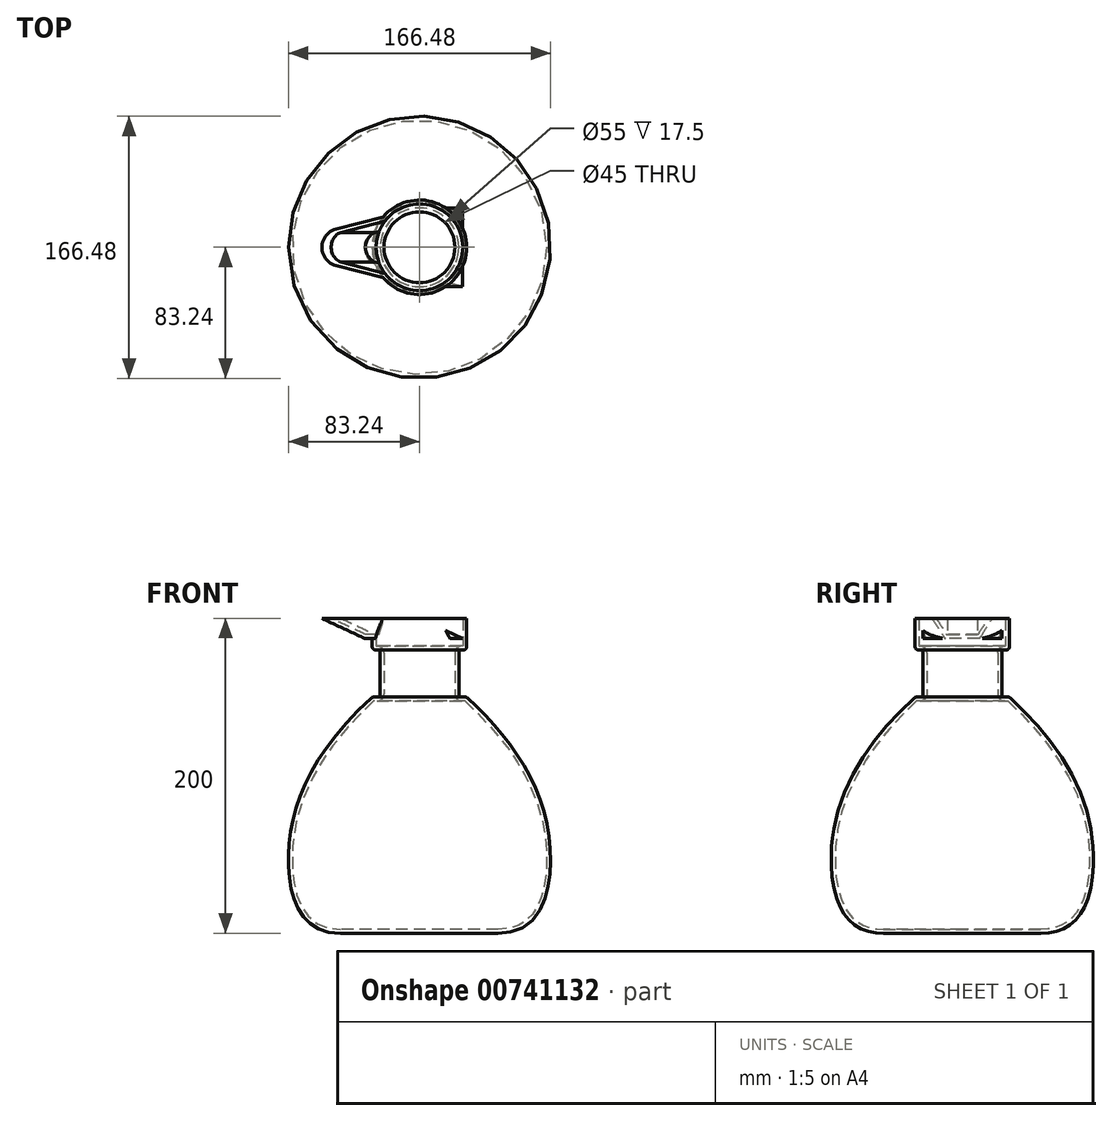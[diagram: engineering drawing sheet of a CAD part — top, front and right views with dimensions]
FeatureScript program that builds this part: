
annotation { "Feature Type Name" : "Feature", "Feature Type Description" : "" }
export const myFeature = defineFeature(function(context is Context, id is Id, definition is map)
    precondition{}
    {
        {
            var Q0;
            Q0=qCreatedBy(makeId("Front.planeOp"),FACE);
            var sketch = newSketch(context, id + "F0", { "sketchPlane" : qUnion([Q0])});
            skLineSegment(sketch, "E0", {"start": v(50, 0) * mm, "end": v(0, 0) * mm});
            skLineSegment(sketch, "E1", {"start": v(0, 0) * mm, "end": v(0, 200) * mm});
            skLineSegment(sketch, "E2", {"start": v(0, 200) * mm, "end": v(30, 200) * mm});
            skLineSegment(sketch, "E3", {"start": v(30, 200) * mm, "end": v(30, 180) * mm});
            skLineSegment(sketch, "E4", {"start": v(30, 180) * mm, "end": v(25, 180) * mm});
            skLineSegment(sketch, "E5", {"start": v(25, 180) * mm, "end": v(25, 150) * mm});
            skLineSegment(sketch, "E6", {"start": v(25, 150) * mm, "end": v(30, 150) * mm});
            skFitSpline(sketch, "E7", {"points": [v(30, 150) * mm, v(83.24, 45.92) * mm, v(50, 0) * mm], "startDerivative": vector(202.96, -186.52) * mm, "endDerivative": vector(-190.27, 0) * mm});
            skSolve(sketch);
        }
        {
            var Q0;
            Q0 = qSketchRegion(id + "F0", true);
            var Q1;
            Q1=sQuery(id+"F0.wireOp",EDGE,"E1");
            revolve(context, id + "F1", {"surfaceOperationType" : NewSurfaceOperationType.NEW, "entities" : qUnion([Q0]), "axis" : qUnion([Q1]), "revolveType" : RevolveType.FULL});
        }
        {
            var Q0;
            Q0=makeQuery(id+"F1.opRevolve","SWEPT_EDGE",EDGE,{"disambiguationData":[OSD([sQuery(id+"F0.wireOp",EDGE,"E3"),sQuery(id+"F0.wireOp",EDGE,"E4")])]});
            var Q1;
            Q1=makeQuery(id+"F1.opRevolve","SWEPT_EDGE",EDGE,{"disambiguationData":[OSD([sQuery(id+"F0.wireOp",EDGE,"E4"),sQuery(id+"F0.wireOp",EDGE,"E5")])]});
            var Q2;
            Q2=makeQuery(id+"F1.opRevolve","SWEPT_EDGE",EDGE,{"disambiguationData":[OSD([sQuery(id+"F0.wireOp",EDGE,"E6"),sQuery(id+"F0.wireOp",EDGE,"E7")])]});
            var Q3;
            Q3=makeQuery(id+"F1.opRevolve","SWEPT_EDGE",EDGE,{"disambiguationData":[OSD([sQuery(id+"F0.wireOp",EDGE,"E5"),sQuery(id+"F0.wireOp",EDGE,"E6")])]});
            fillet(context, id + "F2", {"entities" : qUnion([Q0, Q1, Q2, Q3]), "radius" : 2 * mm, "tangentPropagation" : true, "allowEdgeOverflow" : false});
        }
        {
            var Q0;
            Q0=makeQuery(id+"F1.opRevolve","SWEPT_FACE",FACE,{"disambiguationData":[OSD([sQuery(id+"F0.wireOp",EDGE,"E2")])]});
            var sketch = newSketch(context, id + "F3", { "sketchPlane" : qUnion([Q0])});
            skArc(sketch, "E8", {"start": v(-62, 0) * mm, "mid": v(-59.47, -7.37) * mm, "end": v(-52.94, -11.63) * mm});
            skLineSegment(sketch, "E9", {"start": v(0, 0) * mm, "end": v(0, -25) * mm});
            skLineSegment(sketch, "E10", {"start": v(0, -25) * mm, "end": v(-52.94, -11.63) * mm});
            skLineSegment(sketch, "E11", {"start": v(-62, 0) * mm, "end": v(0, 0) * mm});
            skArc(sketch, "E12.MirrorCS", {"start": v(-62, 0) * mm, "mid": v(-59.47, 7.37) * mm, "end": v(-52.94, 11.63) * mm});
            skLineSegment(sketch, "E13.MirrorCS", {"start": v(0, 25) * mm, "end": v(-52.94, 11.63) * mm});
            skLineSegment(sketch, "E14.MirrorCS", {"start": v(0, 0) * mm, "end": v(0, 25) * mm});
            skSolve(sketch);
        }
        {
            var Q0;
            Q0=qCreatedBy(makeId("Front.planeOp"),FACE);
            var sketch = newSketch(context, id + "F4", { "sketchPlane" : qUnion([Q0])});
            skLineSegment(sketch, "E15", {"start": v(0, 200) * mm, "end": v(27.19, 187.32) * mm});
            skSolve(sketch);
        }
        {
            var Q0;
            Q0 = qSketchRegion(id + "F3", true);
            var Q1;
            Q1 = qConstructionFilter(qBodyType(qCreatedBy(id + "F4" ,EDGE), BodyType.WIRE), ConstructionObject.NO);
            sweep(context, id + "F5", {"operationType" : NewBodyOperationType.ADD, "profiles" : qUnion([Q0]), "path" : qUnion([Q1])});
        }
        {
            var Q0;
            Q0=makeQuery(id+"F5.boolean.opBoolean","MERGE",FACE,{"derivedFrom":[makeQuery(id+"F1.opRevolve","SWEPT_FACE",FACE,{"disambiguationData":[OSD([sQuery(id+"F0.wireOp",EDGE,"E2")])]}),makeQuery(id+"F5.opSweep","CAP_FACE",FACE,{"disambiguationData":[OSD([sQuery(id+"F3.wireOp",EDGE,"E8"),sQuery(id+"F3.wireOp",EDGE,"E9"),sQuery(id+"F3.wireOp",EDGE,"E10"),sQuery(id+"F3.wireOp",EDGE,"E12.MirrorCS"),sQuery(id+"F3.wireOp",EDGE,"E13.MirrorCS"),sQuery(id+"F3.wireOp",EDGE,"E14.MirrorCS"),sQuery(id+"F4.wireOp",VERTEX,"E15.start")])],"isStart":true})]});
            shell(context, id + "F6", {"entities" : qUnion([Q0]), "thickness" : 2.5 * mm});
        }
    });
